# Revit family: Safety & Protection_Barrier_UltiGroup_Pedestrian Barrier
name_source: partatom
category: Generic Models
revit_build: Autodesk Revit Architecture 2016 (Build: 20150220_1215(x64)
units: mm (PartAtom-declared; Revit-internal decimal feet)

## family parameters
Always vertical = Yes
Can host rebar = No
Cut with Voids When Loaded = No
Part Type = Normal
Room Calculation Point = No
Round Connector Dimension = Use Diameter
Shared = No
Work Plane-Based = No

## types (1)
- Type 1
    Barrier Height = 1050 mm
    Barrier Length = 2200 mm  [stored 7.21785 ft]
    Description = Pedestrian Barrier
    Fax = 07 846 2467
    Galvanised Steel = Galvanised Steel Connection
    Galvanised Steel Yellow = Galvanised Steel Connection Yellow
    InstallationGroup_ANZRS = 0
    Left Components (Default) = Yes
    Left Post = Yes
    Manufacturer = UltiGroup
    Model = Ulti Pedestrian Barrier
    ModifiedIssue_ANZRS = 0 $
    Right Components (Default) = Yes
    Right Post = Yes
    Send Message = http://ultigroup.co.nz
    URL = http://ultigroup.co.nz

note: [stored X ft] marks values corroborated as IEEE doubles in the binary element streams (Revit-internal decimal feet)

## geometry (parser evidence)
native form markers: Blend x2, Sweep x8
no freeform markers — native parametric forms only
